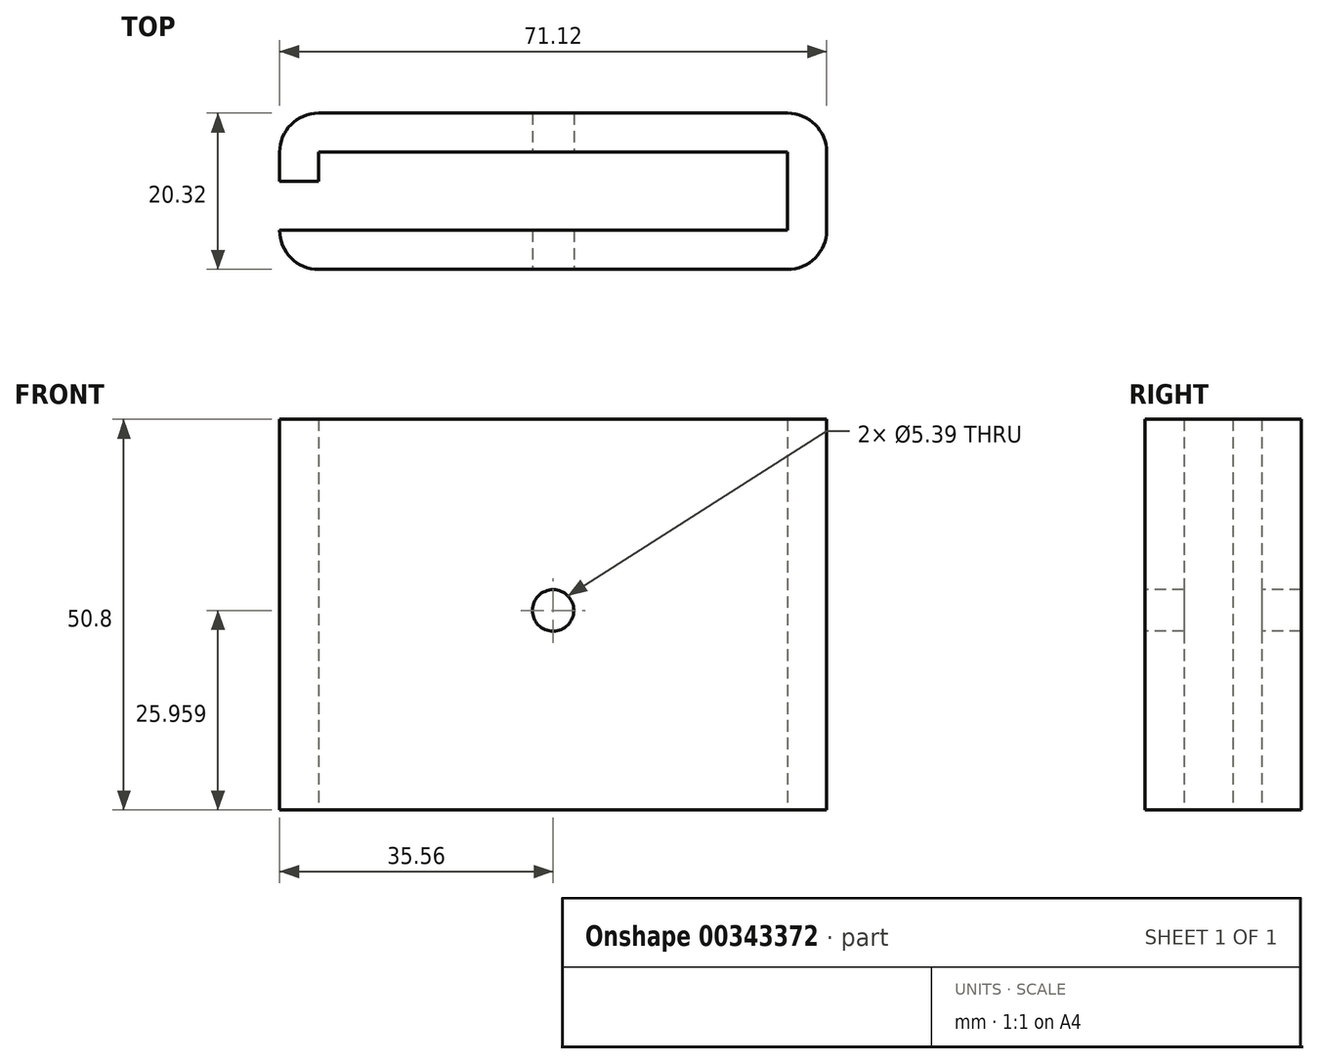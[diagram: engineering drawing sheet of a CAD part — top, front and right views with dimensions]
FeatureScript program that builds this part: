
annotation { "Feature Type Name" : "Feature", "Feature Type Description" : "" }
export const myFeature = defineFeature(function(context is Context, id is Id, definition is map)
    precondition{}
    {
        {
            var Q0;
            Q0=qCreatedBy(makeId("Top.planeOp"),FACE);
            var sketch = newSketch(context, id + "F0", { "sketchPlane" : qUnion([Q0])});
            skLineSegment(sketch, "E0.bottom", {"start": v(-30.48, 5.08) * mm, "end": v(30.48, 5.08) * mm});
            skLineSegment(sketch, "E0.top", {"start": v(-30.48, -5.08) * mm, "end": v(30.48, -5.08) * mm});
            skLineSegment(sketch, "E0.left", {"start": v(-30.48, 5.08) * mm, "end": v(-30.48, -5.08) * mm});
            skLineSegment(sketch, "E0.right", {"start": v(30.48, 5.08) * mm, "end": v(30.48, -5.08) * mm});
            skPoint(sketch, "E0.middle", {"position": v(0, 0) * mm});
            skLineSegment(sketch, "E1", {"start": v(-30.48, 1.27) * mm, "end": v(-35.56, 1.27) * mm});
            skLineSegment(sketch, "E2", {"start": v(-35.56, 1.27) * mm, "end": v(-35.56, 10.16) * mm});
            skLineSegment(sketch, "E3", {"start": v(-35.56, 10.16) * mm, "end": v(35.56, 10.16) * mm});
            skLineSegment(sketch, "E4", {"start": v(35.56, 10.16) * mm, "end": v(35.56, -10.16) * mm});
            skLineSegment(sketch, "E5", {"start": v(35.56, -10.16) * mm, "end": v(-35.56, -10.16) * mm});
            skLineSegment(sketch, "E6", {"start": v(-35.56, -10.16) * mm, "end": v(-35.56, -5.08) * mm});
            skLineSegment(sketch, "E7", {"start": v(-35.56, -5.08) * mm, "end": v(-30.48, -5.08) * mm});
            skSolve(sketch);
        }
        {
            var Q0;
            {var subQ1=sQuery(id+"F0.wireOp",EDGE,"E0.bottom");Q0=makeQuery(id+"F0.imprint","IMPRINT",FACE,{"disambiguationData":[TD([[makeQuery(id+"F0.imprint","IMPRINT",EDGE,{"derivedFrom":subQ1}),1.0]])]});}
            extrude(context, id + "F1", {"entities" : qUnion([Q0]), "depth" : 50.8 * mm});
        }
        {
            var Q0;
            Q0=makeQuery(id+"F1.opExtrude","SWEPT_EDGE",EDGE,{"disambiguationData":[OSD([sQuery(id+"F0.wireOp",EDGE,"E3"),sQuery(id+"F0.wireOp",EDGE,"E4")])]});
            var Q1;
            Q1=makeQuery(id+"F1.opExtrude","SWEPT_EDGE",EDGE,{"disambiguationData":[OSD([sQuery(id+"F0.wireOp",EDGE,"E4"),sQuery(id+"F0.wireOp",EDGE,"E5")])]});
            var Q2;
            Q2=makeQuery(id+"F1.opExtrude","SWEPT_EDGE",EDGE,{"disambiguationData":[OSD([sQuery(id+"F0.wireOp",EDGE,"E2"),sQuery(id+"F0.wireOp",EDGE,"E3")])]});
            var Q3;
            Q3=makeQuery(id+"F1.opExtrude","SWEPT_EDGE",EDGE,{"disambiguationData":[OSD([sQuery(id+"F0.wireOp",EDGE,"E5"),sQuery(id+"F0.wireOp",EDGE,"E6")])]});
            fillet(context, id + "F2", {"entities" : qUnion([Q0, Q1, Q2, Q3]), "radius" : 5.08 * mm, "tangentPropagation" : true, "allowEdgeOverflow" : false});
        }
        {
            var Q0;
            Q0=makeQuery(id+"F1.opExtrude","SWEPT_FACE",FACE,{"disambiguationData":[OSD([sQuery(id+"F0.wireOp",EDGE,"E5")])]});
            var sketch = newSketch(context, id + "F3", { "sketchPlane" : qUnion([Q0])});
            skCircle(sketch, "E8", {"center": v(0, 25.96) * mm, "radius": 2.7 * mm});
            skSolve(sketch);
        }
        {
            var Q0;
            Q0=makeQuery(id+"F3.imprint","IMPRINT",FACE,{"disambiguationData":[TD([[makeQuery(id+"F3.imprint","IMPRINT",EDGE,{"derivedFrom":sQuery(id+"F3.wireOp",EDGE,"E8")}),1.0]])]});
            extrude(context, id + "F4", {"entities" : qUnion([Q0]), "operationType" : NewBodyOperationType.REMOVE, "oppositeDirection" : true, "depth" : 25.4 * mm});
        }
    });
